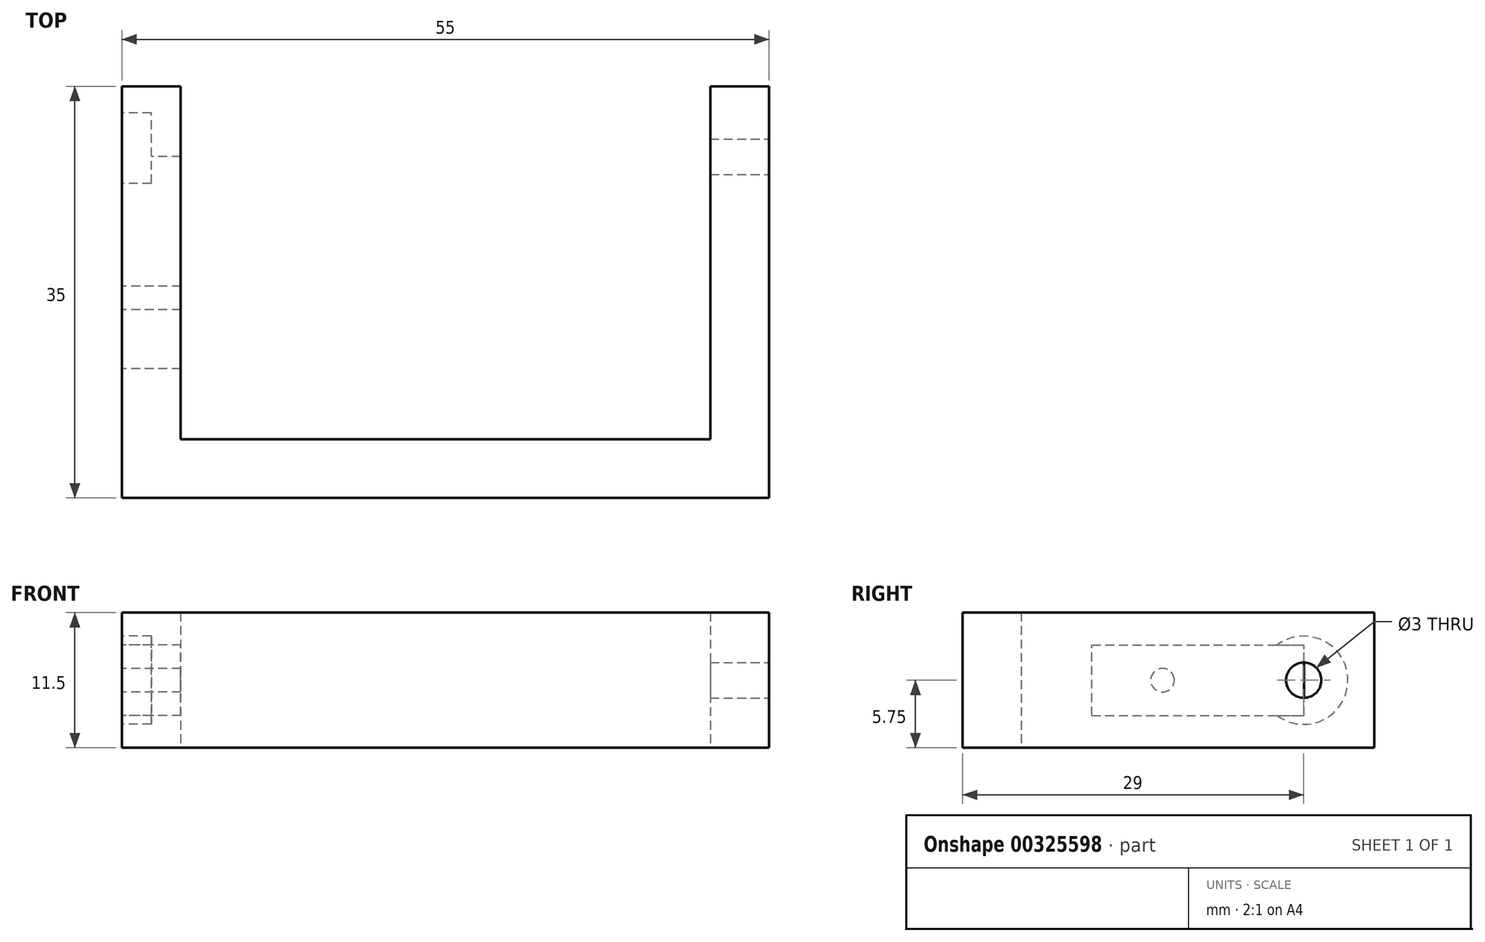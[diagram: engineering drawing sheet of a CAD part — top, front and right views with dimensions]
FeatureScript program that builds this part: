
annotation { "Feature Type Name" : "Feature", "Feature Type Description" : "" }
export const myFeature = defineFeature(function(context is Context, id is Id, definition is map)
    precondition{}
    {
        {
            var Q0;
            Q0=qCreatedBy(makeId("Top.planeOp"),FACE);
            var sketch = newSketch(context, id + "F0", { "sketchPlane" : qUnion([Q0])});
            skLineSegment(sketch, "E0", {"start": v(-23.32, 0) * mm, "end": v(21.68, 0) * mm});
            skLineSegment(sketch, "E1", {"start": v(-23.32, 0) * mm, "end": v(-23.32, 30) * mm});
            skLineSegment(sketch, "E2", {"start": v(21.68, 0) * mm, "end": v(21.68, 30) * mm});
            skLineSegment(sketch, "E3", {"start": v(-23.32, 30) * mm, "end": v(-28.32, 30) * mm});
            skLineSegment(sketch, "E4", {"start": v(-28.32, 30) * mm, "end": v(-28.32, -5) * mm});
            skLineSegment(sketch, "E5", {"start": v(-28.32, -5) * mm, "end": v(26.68, -5) * mm});
            skLineSegment(sketch, "E6", {"start": v(26.68, -5) * mm, "end": v(26.68, 30) * mm});
            skLineSegment(sketch, "E7", {"start": v(26.68, 30) * mm, "end": v(21.68, 30) * mm});
            skSolve(sketch);
        }
        {
            var Q0;
            Q0=makeQuery(id+"F0.imprint","IMPRINT",FACE,{"disambiguationData":[TD([[makeQuery(id+"F0.imprint","IMPRINT",EDGE,{"derivedFrom":sQuery(id+"F0.wireOp",EDGE,"E0")}),-1.0]])]});
            extrude(context, id + "F1", {"entities" : qUnion([Q0]), "depth" : 11.5 * mm});
        }
        {
            var Q0;
            Q0=makeQuery(id+"F1.opExtrude","SWEPT_FACE",FACE,{"disambiguationData":[OSD([sQuery(id+"F0.wireOp",EDGE,"E4")])]});
            var sketch = newSketch(context, id + "F2", { "sketchPlane" : qUnion([Q0])});
            skPoint(sketch, "E8", {"position": v(-30, 5.75) * mm});
            skLineSegment(sketch, "E9", {"start": v(-30, 5.75) * mm, "end": v(-6, 5.75) * mm});
            skPoint(sketch, "E10", {"position": v(-24, 5.75) * mm});
            skCircle(sketch, "E11", {"center": v(-24, 5.75) * mm, "radius": 3.75 * mm});
            skPoint(sketch, "E12", {"position": v(-12, 5.75) * mm});
            skCircle(sketch, "E13", {"center": v(-12, 5.75) * mm, "radius": 1 * mm});
            skLineSegment(sketch, "E14", {"start": v(-6, 0) * mm, "end": v(-6, 11.5) * mm});
            skLineSegment(sketch, "E15.bottom", {"start": v(-6, 2.75) * mm, "end": v(-24.03, 2.75) * mm});
            skLineSegment(sketch, "E15.top", {"start": v(-6, 8.75) * mm, "end": v(-24.03, 8.75) * mm});
            skLineSegment(sketch, "E15.left", {"start": v(-6, 2.75) * mm, "end": v(-6, 8.75) * mm});
            skLineSegment(sketch, "E15.right", {"start": v(-24.03, 2.75) * mm, "end": v(-24.03, 8.75) * mm});
            skSolve(sketch);
        }
        {
            var Q0;
            {var subQ0=sQuery(id+"F2.wireOp",EDGE,"E15.right");var subQ1=sQuery(id+"F2.wireOp",EDGE,"E9");var subQ2=makeQuery(id+"F2.imprint","INTERSECT",VERTEX,{"derivedFrom":[subQ1,subQ0]});Q0=makeQuery(id+"F2.imprint","IMPRINT",FACE,{"disambiguationData":[TD([[makeQuery(id+"F2.imprint","IMPRINT",EDGE,{"disambiguationData":[TD([[subQ2,-1.0]])],"derivedFrom":subQ1}),-1.0]])]});}
            var Q1;
            {var subQ0=sQuery(id+"F2.wireOp",EDGE,"E15.right");var subQ1=sQuery(id+"F2.wireOp",EDGE,"E9");var subQ2=makeQuery(id+"F2.imprint","INTERSECT",VERTEX,{"derivedFrom":[subQ1,subQ0]});Q1=makeQuery(id+"F2.imprint","IMPRINT",FACE,{"disambiguationData":[TD([[makeQuery(id+"F2.imprint","IMPRINT",EDGE,{"disambiguationData":[TD([[subQ2,-1.0]])],"derivedFrom":subQ1}),1.0]])]});}
            var Q2;
            {var subQ0=sQuery(id+"F2.wireOp",EDGE,"E11");var subQ1=sQuery(id+"F2.wireOp",EDGE,"E9");var subQ2=makeQuery(id+"F2.imprint","INTERSECT",VERTEX,{"disambiguationData":[OD(0.0)],"derivedFrom":[subQ1,subQ0]});Q2=makeQuery(id+"F2.imprint","IMPRINT",FACE,{"disambiguationData":[TD([[makeQuery(id+"F2.imprint","IMPRINT",EDGE,{"disambiguationData":[TD([[subQ2,-1.0]])],"derivedFrom":subQ1}),1.0]])]});}
            var Q3;
            {var subQ0=sQuery(id+"F2.wireOp",EDGE,"E11");var subQ1=sQuery(id+"F2.wireOp",EDGE,"E9");var subQ2=makeQuery(id+"F2.imprint","INTERSECT",VERTEX,{"disambiguationData":[OD(0.0)],"derivedFrom":[subQ1,subQ0]});Q3=makeQuery(id+"F2.imprint","IMPRINT",FACE,{"disambiguationData":[TD([[makeQuery(id+"F2.imprint","IMPRINT",EDGE,{"disambiguationData":[TD([[subQ2,-1.0]])],"derivedFrom":subQ1}),-1.0]])]});}
            var Q4;
            {var subQ0=sQuery(id+"F2.wireOp",EDGE,"E13");var subQ1=sQuery(id+"F2.wireOp",EDGE,"E9");var subQ2=makeQuery(id+"F2.imprint","INTERSECT",VERTEX,{"disambiguationData":[OD(0.0)],"derivedFrom":[subQ1,subQ0]});Q4=makeQuery(id+"F2.imprint","IMPRINT",FACE,{"disambiguationData":[TD([[makeQuery(id+"F2.imprint","IMPRINT",EDGE,{"disambiguationData":[TD([[subQ2,-1.0]])],"derivedFrom":subQ1}),-1.0]])]});}
            var Q5;
            {var subQ0=sQuery(id+"F2.wireOp",EDGE,"E13");var subQ1=sQuery(id+"F2.wireOp",EDGE,"E9");var subQ2=makeQuery(id+"F2.imprint","INTERSECT",VERTEX,{"disambiguationData":[OD(0.0)],"derivedFrom":[subQ1,subQ0]});Q5=makeQuery(id+"F2.imprint","IMPRINT",FACE,{"disambiguationData":[TD([[makeQuery(id+"F2.imprint","IMPRINT",EDGE,{"disambiguationData":[TD([[subQ2,-1.0]])],"derivedFrom":subQ1}),1.0]])]});}
            extrude(context, id + "F3", {"entities" : qUnion([Q0, Q1, Q2, Q3, Q4, Q5]), "operationType" : NewBodyOperationType.REMOVE, "oppositeDirection" : true, "depth" : 25 * mm});
        }
        {
            var Q0;
            {var subQ1=sQuery(id+"F2.wireOp",EDGE,"E9");var subQ4=sQuery(id+"F2.wireOp",EDGE,"E11");var subQ5=makeQuery(id+"F2.imprint","INTERSECT",VERTEX,{"disambiguationData":[OD(1.0)],"derivedFrom":[subQ1,subQ4]});Q0=makeQuery(id+"F2.imprint","IMPRINT",FACE,{"disambiguationData":[TD([[makeQuery(id+"F2.imprint","IMPRINT",EDGE,{"disambiguationData":[TD([[subQ5,-1.0]])],"derivedFrom":subQ1}),-1.0]])]});}
            var Q1;
            {var subQ0=sQuery(id+"F2.wireOp",EDGE,"E11");var subQ1=sQuery(id+"F2.wireOp",EDGE,"E9");var subQ2=makeQuery(id+"F2.imprint","INTERSECT",VERTEX,{"disambiguationData":[OD(1.0)],"derivedFrom":[subQ1,subQ0]});Q1=makeQuery(id+"F2.imprint","IMPRINT",FACE,{"disambiguationData":[TD([[makeQuery(id+"F2.imprint","IMPRINT",EDGE,{"disambiguationData":[TD([[subQ2,-1.0]])],"derivedFrom":subQ1}),1.0]])]});}
            extrude(context, id + "F4", {"entities" : qUnion([Q0, Q1]), "operationType" : NewBodyOperationType.REMOVE, "oppositeDirection" : true, "depth" : 2.5 * mm});
        }
        {
            var Q0;
            Q0=makeQuery(id+"F1.opExtrude","SWEPT_FACE",FACE,{"disambiguationData":[OSD([sQuery(id+"F0.wireOp",EDGE,"E6")])]});
            var sketch = newSketch(context, id + "F5", { "sketchPlane" : qUnion([Q0])});
            skPoint(sketch, "E16", {"position": v(30, 5.75) * mm});
            skLineSegment(sketch, "E17", {"start": v(30, 5.75) * mm, "end": v(21.36, 5.75) * mm});
            skPoint(sketch, "E18", {"position": v(24, 5.75) * mm});
            skCircle(sketch, "E19", {"center": v(24, 5.75) * mm, "radius": 1.5 * mm});
            skSolve(sketch);
        }
        {
            var Q0;
            {var subQ0=sQuery(id+"F5.wireOp",EDGE,"E19");var subQ1=sQuery(id+"F5.wireOp",EDGE,"E17");var subQ2=makeQuery(id+"F5.imprint","INTERSECT",VERTEX,{"disambiguationData":[OD(0.0)],"derivedFrom":[subQ1,subQ0]});Q0=makeQuery(id+"F5.imprint","IMPRINT",FACE,{"disambiguationData":[TD([[makeQuery(id+"F5.imprint","IMPRINT",EDGE,{"disambiguationData":[TD([[subQ2,1.0]])],"derivedFrom":subQ1}),-1.0]])]});}
            var Q1;
            {var subQ0=sQuery(id+"F5.wireOp",EDGE,"E19");var subQ1=sQuery(id+"F5.wireOp",EDGE,"E17");var subQ2=makeQuery(id+"F5.imprint","INTERSECT",VERTEX,{"disambiguationData":[OD(0.0)],"derivedFrom":[subQ1,subQ0]});Q1=makeQuery(id+"F5.imprint","IMPRINT",FACE,{"disambiguationData":[TD([[makeQuery(id+"F5.imprint","IMPRINT",EDGE,{"disambiguationData":[TD([[subQ2,1.0]])],"derivedFrom":subQ1}),1.0]])]});}
            extrude(context, id + "F6", {"entities" : qUnion([Q0, Q1]), "operationType" : NewBodyOperationType.REMOVE, "oppositeDirection" : true, "depth" : 25 * mm});
        }
    });
